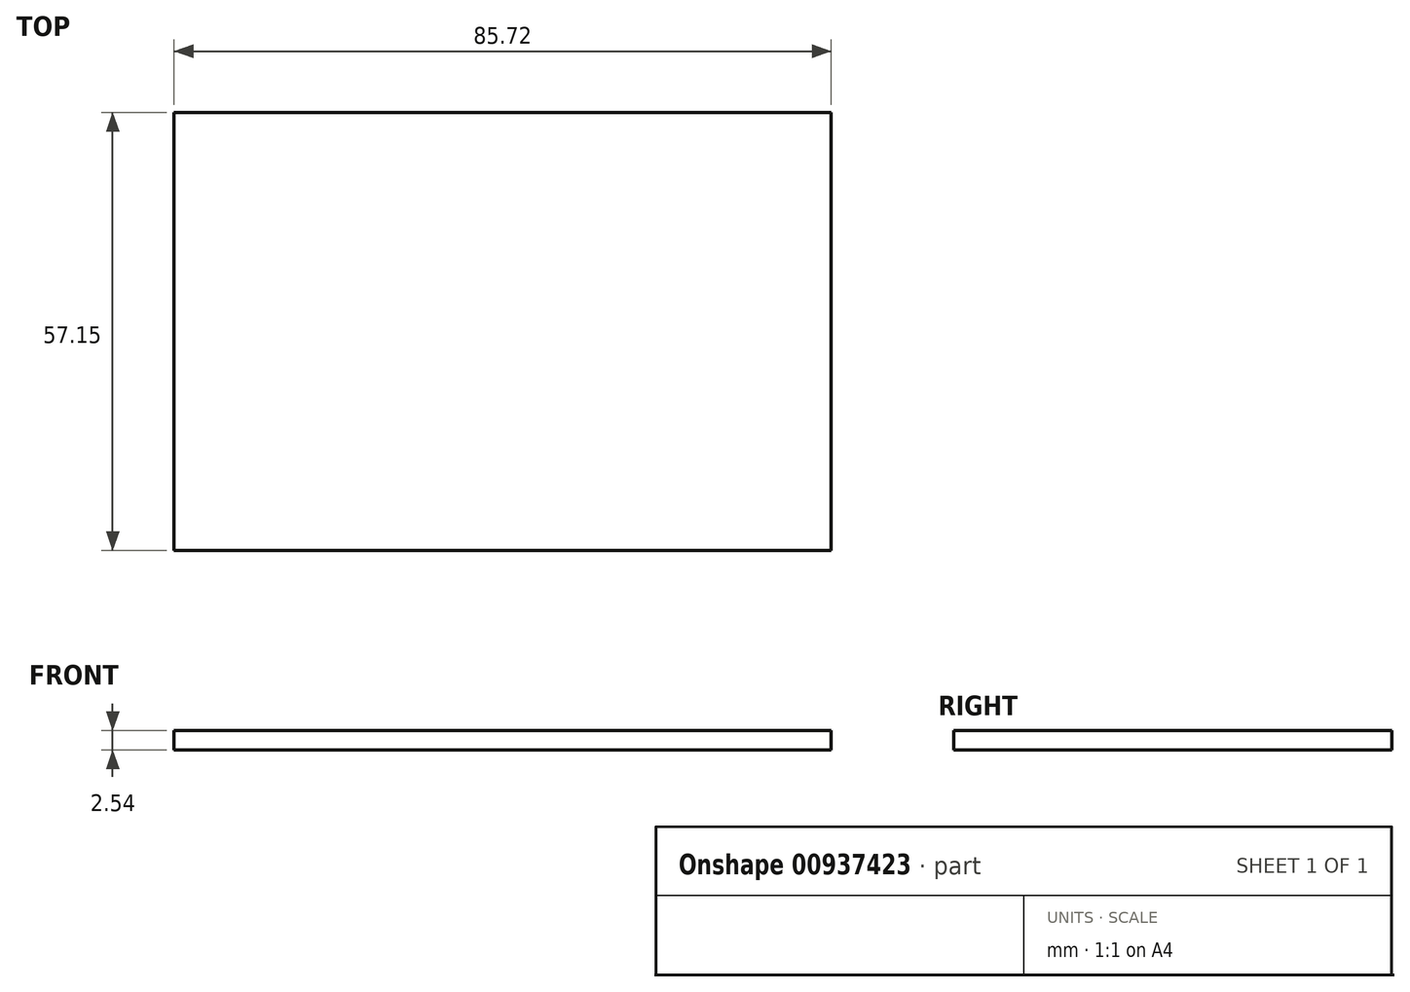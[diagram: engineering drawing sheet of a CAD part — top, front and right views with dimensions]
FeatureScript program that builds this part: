
annotation { "Feature Type Name" : "Feature", "Feature Type Description" : "" }
export const myFeature = defineFeature(function(context is Context, id is Id, definition is map)
    precondition{}
    {
        {
            var Q0;
            Q0=qCreatedBy(makeId("Top.planeOp"),FACE);
            var sketch = newSketch(context, id + "F0", { "sketchPlane" : qUnion([Q0])});
            skLineSegment(sketch, "E0.bottom", {"start": v(0, 0) * mm, "end": v(85.72, 0) * mm});
            skLineSegment(sketch, "E0.top", {"start": v(0, 57.15) * mm, "end": v(85.72, 57.15) * mm});
            skLineSegment(sketch, "E0.left", {"start": v(0, 0) * mm, "end": v(0, 57.15) * mm});
            skLineSegment(sketch, "E0.right", {"start": v(85.72, 0) * mm, "end": v(85.72, 57.15) * mm});
            skSolve(sketch);
        }
        {
            var Q0;
            Q0=makeQuery(id+"F0.imprint","IMPRINT",FACE,{"disambiguationData":[TD([[makeQuery(id+"F0.imprint","IMPRINT",EDGE,{"derivedFrom":sQuery(id+"F0.wireOp",EDGE,"E0.bottom")}),1.0]])]});
            extrude(context, id + "F1", {"entities" : qUnion([Q0]), "depth" : 2.54 * mm, "offsetDistance" : 25.4 * mm});
        }
    });
